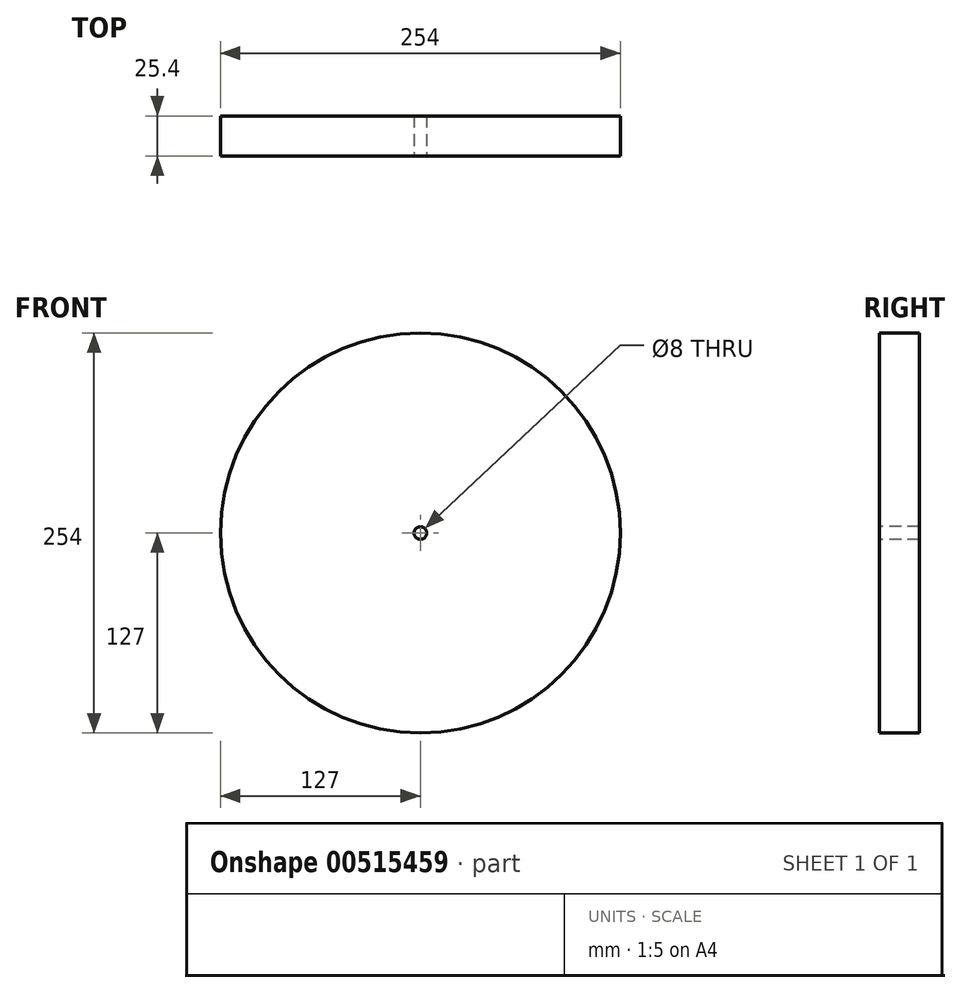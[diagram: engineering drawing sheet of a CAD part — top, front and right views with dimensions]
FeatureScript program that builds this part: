
annotation { "Feature Type Name" : "Feature", "Feature Type Description" : "" }
export const myFeature = defineFeature(function(context is Context, id is Id, definition is map)
    precondition{}
    {
        {
            var Q0;
            Q0=qCreatedBy(makeId("Front.planeOp"),FACE);
            var sketch = newSketch(context, id + "F0", { "sketchPlane" : qUnion([Q0])});
            skCircle(sketch, "E0", {"center": v(0, 0) * mm, "radius": 127 * mm});
            skSolve(sketch);
        }
        {
            var Q0;
            Q0=qSketchRegion(id+"F0",true);
            extrude(context, id + "F1", {"entities" : qUnion([Q0]), "depth" : 25.4 * mm, "offsetDistance" : 25.4 * mm});
        }
        {
            var Q0;
            Q0=makeQuery(id+"F1.opExtrude","CAP_FACE",FACE,{"disambiguationData":[OSD([sQuery(id+"F0.wireOp",EDGE,"E0")])],"isStart":false});
            var sketch = newSketch(context, id + "F2", { "sketchPlane" : qUnion([Q0])});
            skCircle(sketch, "E1", {"center": v(0, 0) * mm, "radius": 4 * mm});
            skSolve(sketch);
        }
        {
            var Q0;
            Q0 = qSketchRegion(id + "F2", true);
            extrude(context, id + "F3", {"entities" : qUnion([Q0]), "operationType" : NewBodyOperationType.REMOVE, "endBound" : BoundingType.THROUGH_ALL, "oppositeDirection" : true, "depth" : 25.4 * mm, "offsetDistance" : 25.4 * mm});
        }
    });
